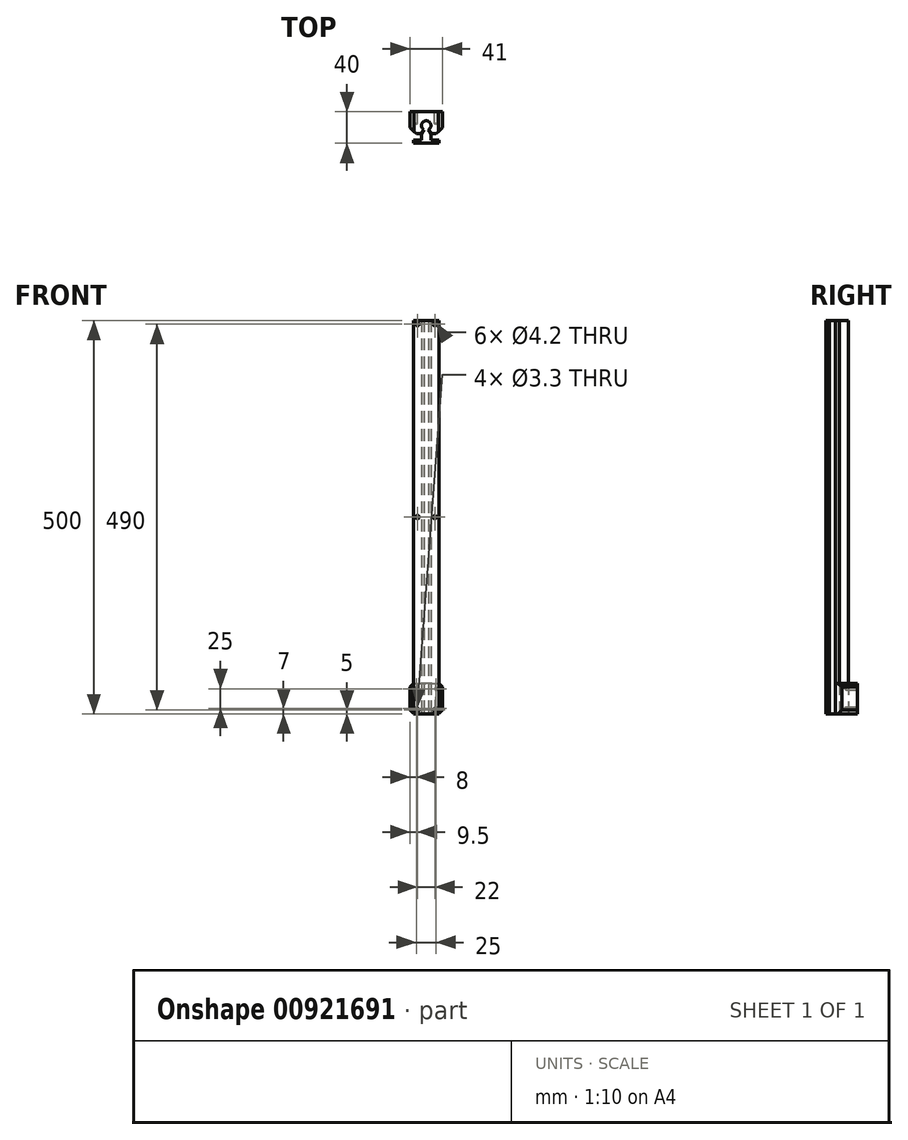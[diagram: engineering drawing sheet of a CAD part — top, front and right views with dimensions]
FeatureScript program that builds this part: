
annotation { "Feature Type Name" : "Feature", "Feature Type Description" : "" }
export const myFeature = defineFeature(function(context is Context, id is Id, definition is map)
    precondition{}
    {
        {
            var Q0;
            Q0=qCreatedBy(makeId("Top.planeOp"),FACE);
            var sketch = newSketch(context, id + "F0", { "sketchPlane" : qUnion([Q0])});
            skCircle(sketch, "E0", {"center": v(0, 22.5) * mm, "radius": 6 * mm});
            skLineSegment(sketch, "E1.bottom", {"start": v(-16, 4) * mm, "end": v(16, 4) * mm});
            skLineSegment(sketch, "E1.top", {"start": v(-16, 0) * mm, "end": v(16, 0) * mm});
            skLineSegment(sketch, "E1.left", {"start": v(-16, 4) * mm, "end": v(-16, 0) * mm});
            skLineSegment(sketch, "E1.right", {"start": v(16, 4) * mm, "end": v(16, 0) * mm});
            skLineSegment(sketch, "E2", {"start": v(0, 22.5) * mm, "end": v(0, 0) * mm, "construction": true});
            skPoint(sketch, "E3", {"position": v(-3, 17.3) * mm});
            skLineSegment(sketch, "E4", {"start": v(-3, 17.3) * mm, "end": v(-6.06, 12) * mm});
            skLineSegment(sketch, "E5", {"start": v(-6.06, 12) * mm, "end": v(-6.06, 4) * mm});
            skLineSegment(sketch, "E6.MirrorCS", {"start": v(3, 17.3) * mm, "end": v(6.06, 12) * mm});
            skLineSegment(sketch, "E7.MirrorCS", {"start": v(6.06, 12) * mm, "end": v(6.06, 4) * mm});
            skLineSegment(sketch, "E8", {"start": v(-20.5, 12) * mm, "end": v(-20.5, 40) * mm});
            skLineSegment(sketch, "E9", {"start": v(-20.5, 40) * mm, "end": v(20.5, 40) * mm});
            skLineSegment(sketch, "E10", {"start": v(20.5, 40) * mm, "end": v(20.5, 12) * mm});
            skLineSegment(sketch, "E11", {"start": v(0, 22.5) * mm, "end": v(0, 40) * mm, "construction": true});
            skLineSegment(sketch, "E12", {"start": v(-20.5, 12) * mm, "end": v(-6.06, 12) * mm});
            skLineSegment(sketch, "E13", {"start": v(6.06, 12) * mm, "end": v(20.5, 12) * mm});
            skSolve(sketch);
        }
        {
            var Q0;
            {var subQ0=sQuery(id+"F0.wireOp",EDGE,"E0");var subQ1=makeQuery(id+"F0.imprint","INTERSECT",VERTEX,{"derivedFrom":[subQ0,sQuery(id+"F0.wireOp",EDGE,"E4")]});Q0=makeQuery(id+"F0.imprint","IMPRINT",FACE,{"disambiguationData":[TD([[makeQuery(id+"F0.imprint","IMPRINT",EDGE,{"disambiguationData":[TD([[subQ1,-1.0]])],"derivedFrom":subQ0}),1.0]])]});}
            var Q1;
            {var subQ1=sQuery(id+"F0.wireOp",EDGE,"E4");Q1=makeQuery(id+"F0.imprint","IMPRINT",FACE,{"disambiguationData":[TD([[makeQuery(id+"F0.imprint","IMPRINT",EDGE,{"derivedFrom":subQ1}),1.0]])]});}
            var Q2;
            Q2=makeQuery(id+"F0.imprint","IMPRINT",FACE,{"disambiguationData":[TD([[makeQuery(id+"F0.imprint","IMPRINT",EDGE,{"derivedFrom":sQuery(id+"F0.wireOp",EDGE,"E1.top")}),1.0]])]});
            extrude(context, id + "F1", {"entities" : qUnion([Q0, Q1, Q2]), "depth" : 500 * mm, "offsetDistance" : 25 * mm});
        }
        {
            var Q0;
            {var subQ0=sQuery(id+"F0.wireOp",EDGE,"E4");Q0=makeQuery(id+"F0.imprint","IMPRINT",FACE,{"disambiguationData":[TD([[makeQuery(id+"F0.imprint","IMPRINT",EDGE,{"derivedFrom":subQ0}),-1.0]])]});}
            extrude(context, id + "F2", {"entities" : qUnion([Q0]), "depth" : 39 * mm, "offsetDistance" : 25 * mm});
        }
        {
            var Q0;
            Q0=makeQuery(id+"F2.opExtrude","SWEPT_FACE",FACE,{"disambiguationData":[OSD([sQuery(id+"F0.wireOp",EDGE,"E9")])]});
            var sketch = newSketch(context, id + "F3", { "sketchPlane" : qUnion([Q0])});
            skLineSegment(sketch, "E14.bottom", {"start": v(-12.5, 32) * mm, "end": v(12.5, 32) * mm});
            skLineSegment(sketch, "E14.top", {"start": v(-12.5, 7) * mm, "end": v(12.5, 7) * mm});
            skLineSegment(sketch, "E14.left", {"start": v(-12.5, 32) * mm, "end": v(-12.5, 7) * mm});
            skLineSegment(sketch, "E14.right", {"start": v(12.5, 32) * mm, "end": v(12.5, 7) * mm});
            skSolve(sketch);
        }
        {
            var Q0;
            Q0=sQuery(id+"F3.wireOp",VERTEX,"E14.bottom.start");
            var Q1;
            Q1=sQuery(id+"F3.wireOp",VERTEX,"E14.top.start");
            var Q2;
            Q2=sQuery(id+"F3.wireOp",VERTEX,"E14.top.end");
            var Q3;
            Q3=sQuery(id+"F3.wireOp",VERTEX,"E14.bottom.end");
            var Q4;
            Q4=makeQuery(id+"F2.opExtrude","SWEPT_BODY",BODY,{"disambiguationData":[OSD([sQuery(id+"F0.wireOp",EDGE,"E0"),sQuery(id+"F0.wireOp",EDGE,"E4"),sQuery(id+"F0.wireOp",EDGE,"E6.MirrorCS"),sQuery(id+"F0.wireOp",EDGE,"E8"),sQuery(id+"F0.wireOp",EDGE,"E9"),sQuery(id+"F0.wireOp",EDGE,"E10"),sQuery(id+"F0.wireOp",EDGE,"E12"),sQuery(id+"F0.wireOp",EDGE,"E13")])]});
            hole(context, id + "F4", {"style" : HoleStyle.SIMPLE, "endStyle" : HoleEndStyle.BLIND, "standardTappedOrClearance" : lookupTablePath({ "standard" : "ISO", "engagement" : "75%", "pitch" : "0.7 mm", "size" : "M4", "type" : "Tapped" }), "standardBlindInLast" : lookupTablePath({ "standard" : "ISO", "engagement" : "75%", "pitch" : "0.7 mm", "size" : "M4", "type" : "Tapped" }), "holeDiameter" : 3.3 * mm, "majorDiameter" : 4 * mm, "showTappedDepth" : true, "holeDepth" : 15 * mm, "tappedDepth" : 12.9 * mm, "tapClearance" : 3, "locations" : qUnion([Q0, Q1, Q2, Q3]), "scope" : qUnion([Q4])});
        }
        {
            var Q0;
            Q0=makeQuery(id+"F2.opExtrude","SWEPT_EDGE",EDGE,{"disambiguationData":[OSD([sQuery(id+"F0.wireOp",EDGE,"E10"),sQuery(id+"F0.wireOp",EDGE,"E13")])]});
            var Q1;
            Q1=makeQuery(id+"F2.opExtrude","SWEPT_EDGE",EDGE,{"disambiguationData":[OSD([sQuery(id+"F0.wireOp",EDGE,"E8"),sQuery(id+"F0.wireOp",EDGE,"E12")])]});
            chamfer(context, id + "F5", {"entities" : qUnion([Q0, Q1]), "width" : 8 * mm, "tangentPropagation" : true});
        }
        {
            var Q0;
            Q0=makeQuery(id+"F2.opExtrude","CAP_EDGE",EDGE,{"disambiguationData":[OSD([sQuery(id+"F0.wireOp",EDGE,"E10")])],"isStart":false});
            var Q1;
            Q1=makeQuery(id+"F2.opExtrude","CAP_EDGE",EDGE,{"disambiguationData":[OSD([sQuery(id+"F0.wireOp",EDGE,"E10")])],"isStart":true});
            var Q2;
            Q2=makeQuery(id+"F2.opExtrude","CAP_EDGE",EDGE,{"disambiguationData":[OSD([sQuery(id+"F0.wireOp",EDGE,"E8")])],"isStart":true});
            var Q3;
            Q3=makeQuery(id+"F2.opExtrude","CAP_EDGE",EDGE,{"disambiguationData":[OSD([sQuery(id+"F0.wireOp",EDGE,"E8")])],"isStart":false});
            chamfer(context, id + "F6", {"entities" : qUnion([Q0, Q1, Q2, Q3]), "width" : 5 * mm, "tangentPropagation" : true});
        }
        {
            var Q0;
            Q0=makeQuery(id+"F1.opExtrude","SWEPT_FACE",FACE,{"disambiguationData":[OSD([sQuery(id+"F0.wireOp",EDGE,"E1.top")])]});
            var sketch = newSketch(context, id + "F7", { "sketchPlane" : qUnion([Q0])});
            skLineSegment(sketch, "E15.bottom", {"start": v(11, 5) * mm, "end": v(-11, 5) * mm});
            skLineSegment(sketch, "E15.top", {"start": v(11, 495) * mm, "end": v(-11, 495) * mm});
            skLineSegment(sketch, "E15.left", {"start": v(11, 5) * mm, "end": v(11, 495) * mm});
            skLineSegment(sketch, "E15.right", {"start": v(-11, 5) * mm, "end": v(-11, 495) * mm});
            skPoint(sketch, "E16", {"position": v(-11, 250) * mm});
            skPoint(sketch, "E17", {"position": v(11, 250) * mm});
            skSolve(sketch);
        }
        {
            var Q0;
            Q0=sQuery(id+"F7.wireOp",VERTEX,"E15.bottom.start");
            var Q1;
            Q1=sQuery(id+"F7.wireOp",VERTEX,"E15.bottom.end");
            var Q2;
            Q2=sQuery(id+"F7.wireOp",VERTEX,"E17");
            var Q3;
            Q3=sQuery(id+"F7.wireOp",VERTEX,"E16");
            var Q4;
            Q4=sQuery(id+"F7.wireOp",VERTEX,"E15.top.start");
            var Q5;
            Q5=sQuery(id+"F7.wireOp",VERTEX,"E15.top.end");
            var Q6;
            Q6=makeQuery(id+"F2.opExtrude","SWEPT_BODY",BODY,{"disambiguationData":[OSD([sQuery(id+"F0.wireOp",EDGE,"E0"),sQuery(id+"F0.wireOp",EDGE,"E4"),sQuery(id+"F0.wireOp",EDGE,"E6.MirrorCS"),sQuery(id+"F0.wireOp",EDGE,"E8"),sQuery(id+"F0.wireOp",EDGE,"E9"),sQuery(id+"F0.wireOp",EDGE,"E10"),sQuery(id+"F0.wireOp",EDGE,"E12"),sQuery(id+"F0.wireOp",EDGE,"E13")])]});
            var Q7;
            Q7=makeQuery(id+"F1.opExtrude","SWEPT_BODY",BODY,{"disambiguationData":[OSD([sQuery(id+"F0.wireOp",EDGE,"E0"),sQuery(id+"F0.wireOp",EDGE,"E1.bottom"),sQuery(id+"F0.wireOp",EDGE,"E1.top"),sQuery(id+"F0.wireOp",EDGE,"E1.left"),sQuery(id+"F0.wireOp",EDGE,"E1.right"),sQuery(id+"F0.wireOp",EDGE,"E4"),sQuery(id+"F0.wireOp",EDGE,"E5"),sQuery(id+"F0.wireOp",EDGE,"E6.MirrorCS"),sQuery(id+"F0.wireOp",EDGE,"E7.MirrorCS")])]});
            hole(context, id + "F8", {"style" : HoleStyle.SIMPLE, "endStyle" : HoleEndStyle.BLIND, "standardTappedOrClearance" : lookupTablePath({ "fit" : "Close", "standard" : "ISO", "size" : "M4", "type" : "Clearance" }), "standardBlindInLast" : lookupTablePath({ "fit" : "Close", "standard" : "ISO", "size" : "M4", "type" : "Clearance" }), "holeDiameter" : 4.2 * mm, "majorDiameter" : 4 * mm, "holeDepth" : 7 * mm, "tappedDepth" : 12.9 * mm, "tapClearance" : 3, "locations" : qUnion([Q0, Q1, Q2, Q3, Q4, Q5]), "scope" : qUnion([Q6, Q7])});
        }
    });
